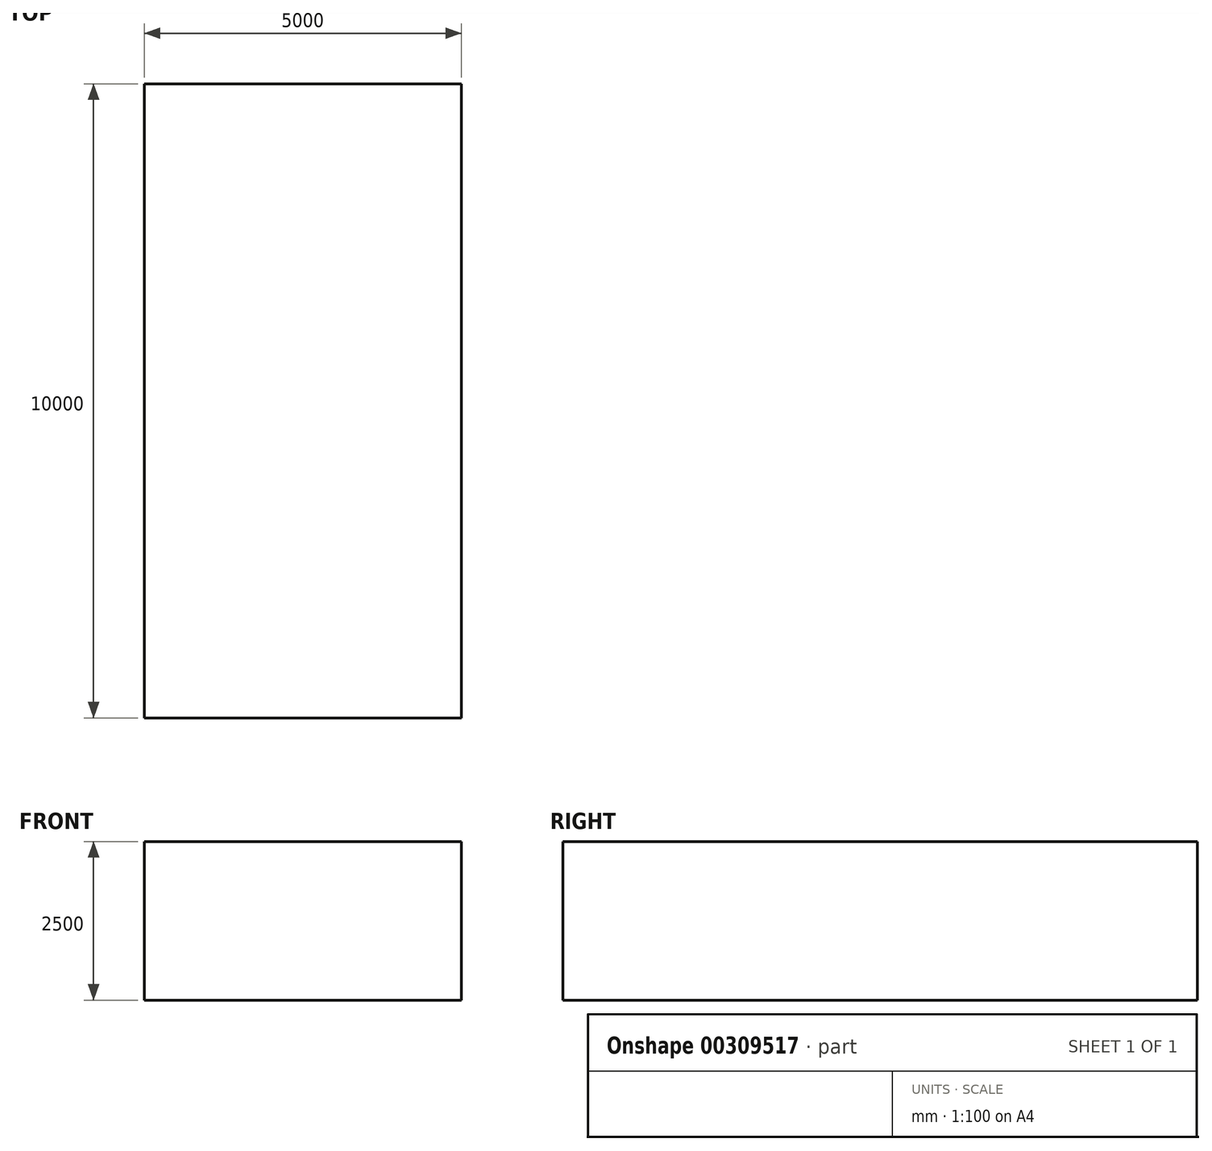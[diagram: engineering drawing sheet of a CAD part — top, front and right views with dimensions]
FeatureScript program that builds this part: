
annotation { "Feature Type Name" : "Feature", "Feature Type Description" : "" }
export const myFeature = defineFeature(function(context is Context, id is Id, definition is map)
    precondition{}
    {
        {
            var Q0;
            Q0=qCreatedBy(makeId("Front.planeOp"),FACE);
            var sketch = newSketch(context, id + "F0", { "sketchPlane" : qUnion([Q0])});
            skLineSegment(sketch, "E0.bottom", {"start": v(0, 0) * mm, "end": v(5000, 0) * mm});
            skLineSegment(sketch, "E0.top", {"start": v(0, 2500) * mm, "end": v(5000, 2500) * mm});
            skLineSegment(sketch, "E0.left", {"start": v(0, 0) * mm, "end": v(0, 2500) * mm});
            skLineSegment(sketch, "E0.right", {"start": v(5000, 0) * mm, "end": v(5000, 2500) * mm});
            skSolve(sketch);
        }
        {
            var Q0;
            Q0=makeQuery(id+"F0.imprint","IMPRINT",FACE,{"disambiguationData":[TD([[makeQuery(id+"F0.imprint","IMPRINT",EDGE,{"derivedFrom":sQuery(id+"F0.wireOp",EDGE,"E0.bottom")}),1.0]])]});
            extrude(context, id + "F1", {"entities" : qUnion([Q0]), "oppositeDirection" : true, "depth" : 10000 * mm});
        }
    });
